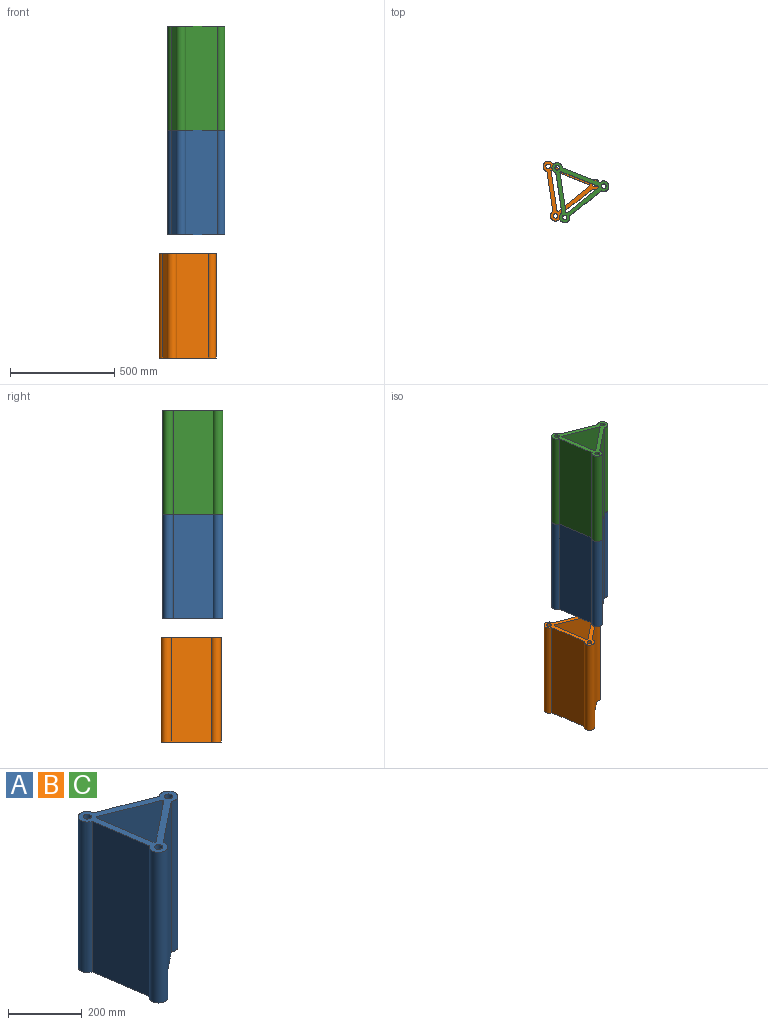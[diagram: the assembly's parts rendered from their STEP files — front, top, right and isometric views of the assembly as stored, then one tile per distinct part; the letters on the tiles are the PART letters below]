
ASSEMBLY  parts=3 mates=1
PART A: 17 faces, bbox 273.3x287.3x500 mm
  f0: cylinder r=25mm len=500mm, axis (0,0,-1), area 55161.9mm2, adj f1,f11,f12,f13
  f1: plane 500x192.03mm, normal (-0.99,-0.15,0), area 97087.1mm2, adj f0,f2,f12,f13
  f2: cylinder r=25mm len=500mm, axis (0,0,-1), area 55161.9mm2, adj f1,f3,f12,f13
  f3: plane 500x151.91mm, normal (0.62,-0.78,0), area 97087.1mm2, adj f2,f4,f12,f13
  f4: cylinder r=25mm len=500mm, axis (0,0,-1), area 55161.9mm2, adj f3,f11,f12,f13
  f5: plane 500x192.03mm, normal (0.99,0.15,0), area 97087.1mm2, adj f6,f10,f12,f13
  f6: cylinder r=25mm len=500mm, axis (0,0,-1), area 2802mm2, adj f5,f7,f12,f13
  f7: plane 500x180.7mm, normal (-0.37,-0.93,0), area 97087.1mm2, adj f6,f8,f12,f13
  f8: cylinder r=25mm len=500mm, axis (0,0,-1), area 2802mm2, adj f7,f9,f12,f13
  f9: plane 500x151.91mm, normal (-0.62,0.78,0), area 97087.1mm2, adj f8,f10,f12,f13
  f10: cylinder r=25mm len=500mm, axis (0,0,-1), area 2802mm2, adj f5,f9,f12,f13
  f11: plane 500x180.7mm, normal (0.37,0.93,0), area 97087.1mm2, adj f0,f4,f12,f13
  f12: plane 287.35x273.34mm, normal (0,0,1), area 16232.1mm2, adj f0,f1,f2,f3,f4,f5,f6,f7
  f13: plane 287.35x273.34mm, normal (0,0,-1), area 16232.1mm2, adj f0,f1,f2,f3,f4,f5,f6,f7
  f14: cylinder r=11mm len=500mm, axis (0,0,1), area 34557.5mm2, adj f12,f13
  f15: cylinder r=11mm len=500mm, axis (0,0,1), area 34557.5mm2, adj f12,f13
  f16: cylinder r=11mm len=500mm, axis (0,0,1), area 34557.5mm2, adj f12,f13
PART B: same geometry as A
PART C: same geometry as A
PLACE A t=(108.53,21.81,345.44)mm
PLACE B t=(65.56,30.81,-245.97)mm
PLACE C t=(108.53,21.81,845.44)mm
MATE fastened A.f12 <-> C.f13  axis (0,0,1) through (14.13,1.27,845.44)mm
